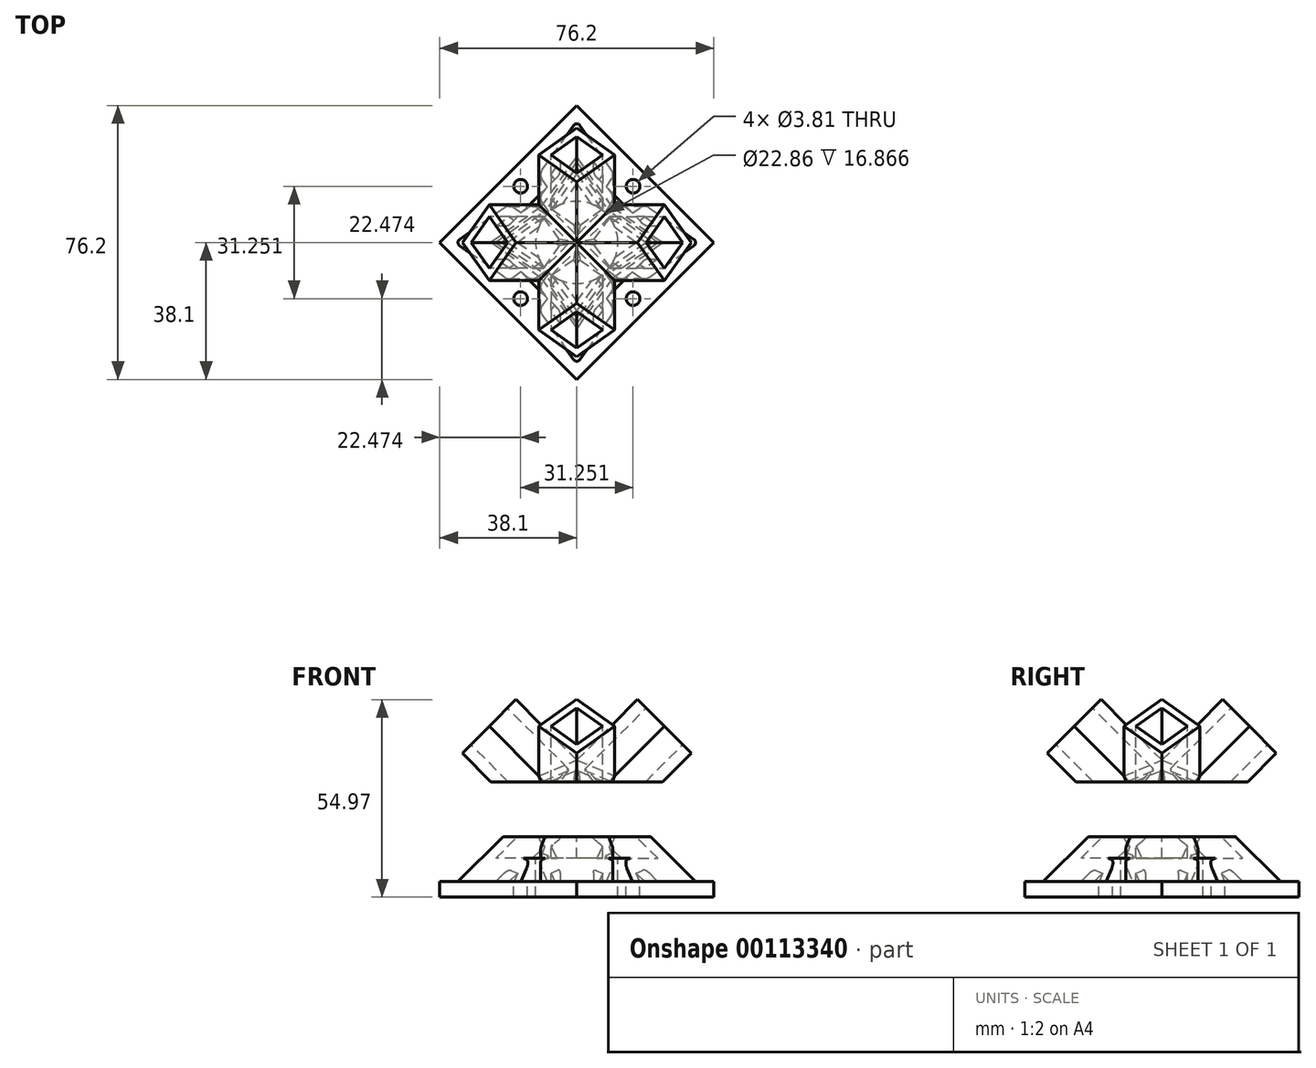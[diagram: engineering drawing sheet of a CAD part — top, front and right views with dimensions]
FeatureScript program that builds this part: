
annotation { "Feature Type Name" : "Feature", "Feature Type Description" : "" }
export const myFeature = defineFeature(function(context is Context, id is Id, definition is map)
    precondition{}
    {
        {
            var Q0;
            Q0=qCreatedBy(makeId("Top.planeOp"),FACE);
            var sketch = newSketch(context, id + "F0", { "sketchPlane" : qUnion([Q0])});
            skLineSegment(sketch, "E0", {"start": v(0, 0) * mm, "end": v(0, 35.93) * mm, "construction": true});
            skLineSegment(sketch, "E1", {"start": v(0, 0) * mm, "end": v(30.29, 0) * mm, "construction": true});
            skLineSegment(sketch, "E2", {"start": v(0, 0) * mm, "end": v(34.43, 34.43) * mm, "construction": true});
            skLineSegment(sketch, "E3", {"start": v(0, 38.1) * mm, "end": v(38.1, 0) * mm});
            skLineSegment(sketch, "E4", {"start": v(38.1, 0) * mm, "end": v(0, -38.1) * mm});
            skLineSegment(sketch, "E5", {"start": v(0, -38.1) * mm, "end": v(-38.1, 0) * mm});
            skLineSegment(sketch, "E6", {"start": v(-38.1, 0) * mm, "end": v(0, 38.1) * mm});
            skSolve(sketch);
        }
        {
            var Q0;
            Q0 = qSketchRegion(id + "F0", true);
            extrude(context, id + "F1", {"entities" : qUnion([Q0]), "depth" : 4.32 * mm});
        }
        {
            var Q0;
            Q0=sQuery(id+"F0.wireOp",EDGE,"E1");
            var Q1;
            Q1=qCreatedBy(makeId("Top.planeOp"),FACE);
            cPlane(context, id + "F2", {"entities" : qUnion([Q0, Q1]), "cplaneType" : CPlaneType.LINE_ANGLE, "offset" : 25.4 * mm, "angle" : 45 * degree, "width" : 152.4 * mm, "height" : 152.4 * mm});
        }
        {
            var Q0;
            Q0=qCreatedBy(id+"F2.planeOp",FACE);
            cPlane(context, id + "F3", {"entities" : qUnion([Q0]), "cplaneType" : CPlaneType.OFFSET, "offset" : 50.8 * mm, "oppositeDirection" : true, "width" : 152.4 * mm, "height" : 152.4 * mm});
        }
        {
            var Q0;
            Q0=qCreatedBy(makeId("Right.planeOp"),FACE);
            var sketch = newSketch(context, id + "F4", { "sketchPlane" : qUnion([Q0])});
            skLineSegment(sketch, "E7", {"start": v(0, 0) * mm, "end": v(0, 27.83) * mm, "construction": true});
            skLineSegment(sketch, "E8", {"start": v(-38.1, 0) * mm, "end": v(-56.06, 17.96) * mm, "construction": true});
            skSolve(sketch);
        }
        {
            var Q0;
            Q0=qCreatedBy(id+"F3.planeOp",FACE);
            var sketch = newSketch(context, id + "F5", { "sketchPlane" : qUnion([Q0])});
            skLineSegment(sketch, "E9", {"start": v(0, 26.94) * mm, "end": v(-10.56, 16.38) * mm});
            skLineSegment(sketch, "E10", {"start": v(0, 26.94) * mm, "end": v(0, 0) * mm, "construction": true});
            skLineSegment(sketch, "E11", {"start": v(-10.56, 16.38) * mm, "end": v(0, 5.82) * mm});
            skLineSegment(sketch, "E12", {"start": v(0, 26.94) * mm, "end": v(10.56, 16.38) * mm});
            skLineSegment(sketch, "E13", {"start": v(10.56, 16.38) * mm, "end": v(0, 5.82) * mm});
            skLineSegment(sketch, "E14", {"start": v(0, 23.56) * mm, "end": v(7.18, 16.38) * mm});
            skLineSegment(sketch, "E15", {"start": v(7.18, 16.38) * mm, "end": v(0, 9.2) * mm});
            skLineSegment(sketch, "E16", {"start": v(0, 9.2) * mm, "end": v(-7.18, 16.38) * mm});
            skLineSegment(sketch, "E17", {"start": v(-7.18, 16.38) * mm, "end": v(0, 23.56) * mm});
            skSolve(sketch);
        }
        {
            var Q0;
            Q0=makeQuery(id+"F5.imprint","IMPRINT",FACE,{"disambiguationData":[TD([[makeQuery(id+"F5.imprint","IMPRINT",EDGE,{"derivedFrom":sQuery(id+"F5.wireOp",EDGE,"E9")}),1.0]])]});
            extrude(context, id + "F6", {"entities" : qUnion([Q0]), "operationType" : NewBodyOperationType.ADD, "endBound" : BoundingType.UP_TO_NEXT, "depth" : 25.4 * mm});
        }
        {
            var Q0;
            Q0=makeQuery(id+"F6.opExtrude","SWEPT_FACE",FACE,{"disambiguationData":[OSD([sQuery(id+"F5.wireOp",EDGE,"E11")])]});
            cPlane(context, id + "F7", {"entities" : qUnion([Q0]), "cplaneType" : CPlaneType.OFFSET, "offset" : 0 * mm, "width" : 152.4 * mm, "height" : 152.4 * mm});
        }
        {
            var Q0;
            Q0=qCreatedBy(id+"F7.planeOp",FACE);
            var sketch = newSketch(context, id + "F8", { "sketchPlane" : qUnion([Q0])});
            skLineSegment(sketch, "E18", {"start": v(30.54, 7.4) * mm, "end": v(48.17, 19.87) * mm, "construction": true});
            skCircle(sketch, "E19.cCircle", {"center": v(30.54, 7.4) * mm, "radius": 1.65 * mm, "construction": true});
            skLineSegment(sketch, "E19.0", {"start": v(32.27, 6.6) * mm, "end": v(30.71, 5.5) * mm});
            skLineSegment(sketch, "E19.1", {"start": v(30.71, 5.5) * mm, "end": v(28.98, 6.3) * mm});
            skLineSegment(sketch, "E19.2", {"start": v(28.98, 6.3) * mm, "end": v(28.8, 8.2) * mm});
            skLineSegment(sketch, "E19.3", {"start": v(28.8, 8.2) * mm, "end": v(30.36, 9.3) * mm});
            skLineSegment(sketch, "E19.4", {"start": v(30.36, 9.3) * mm, "end": v(32.1, 8.5) * mm});
            skLineSegment(sketch, "E19.5", {"start": v(32.1, 8.5) * mm, "end": v(32.27, 6.6) * mm});
            skPoint(sketch, "E19.0.midPoint", {"position": v(31.5, 6.06) * mm});
            skSolve(sketch);
        }
        {
            var Q0;
            Q0 = qSketchRegion(id + "F8", true);
            extrude(context, id + "F9", {"entities" : qUnion([Q0]), "operationType" : NewBodyOperationType.REMOVE, "oppositeDirection" : true, "depth" : 2.54 * mm});
        }
        {
            var Q0;
            Q0=makeQuery(id+"F1.opExtrude","SWEPT_BODY",BODY,{"disambiguationData":[OSD([sQuery(id+"F0.wireOp",EDGE,"E3"),sQuery(id+"F0.wireOp",EDGE,"E4"),sQuery(id+"F0.wireOp",EDGE,"E5"),sQuery(id+"F0.wireOp",EDGE,"E6")])]});
            var Q1;
            Q1=sQuery(id+"F4.wireOp",EDGE,"E7");
            circularPattern(context, id + "F10", {"entities" : qUnion([Q0]), "axis" : qUnion([Q1]), "angle" : 90 * degree, "instanceCount" : 4});
        }
        {
            var Q0;
            Q0=qCreatedBy(makeId("Top.planeOp"),FACE);
            cPlane(context, id + "F11", {"entities" : qUnion([Q0]), "cplaneType" : CPlaneType.OFFSET, "offset" : 25.4 * mm, "width" : 152.4 * mm, "height" : 152.4 * mm});
        }
        {
            var Q0;
            Q0=qCreatedBy(id+"F11.planeOp",FACE);
            var sketch = newSketch(context, id + "F12", { "sketchPlane" : qUnion([Q0])});
            skCircle(sketch, "E20", {"center": v(0, 0) * mm, "radius": 11.43 * mm});
            skSolve(sketch);
        }
        {
            var Q0;
            Q0=qCreatedBy(makeId("Top.planeOp"),FACE);
            var sketch = newSketch(context, id + "F13", { "sketchPlane" : qUnion([Q0])});
            skLineSegment(sketch, "E21.bottom", {"start": v(19.05, 19.05) * mm, "end": v(-19.05, 19.05) * mm});
            skLineSegment(sketch, "E21.top", {"start": v(19.05, -19.05) * mm, "end": v(-19.05, -19.05) * mm});
            skLineSegment(sketch, "E21.left", {"start": v(19.05, 19.05) * mm, "end": v(19.05, -19.05) * mm});
            skLineSegment(sketch, "E21.right", {"start": v(-19.05, 19.05) * mm, "end": v(-19.05, -19.05) * mm});
            skPoint(sketch, "E21.middle", {"position": v(0, 0) * mm});
            skLineSegment(sketch, "E22", {"start": v(-19.05, 4.6) * mm, "end": v(-4.6, 19.05) * mm});
            skLineSegment(sketch, "E23", {"start": v(-19.05, -4.6) * mm, "end": v(-4.6, -19.05) * mm});
            skLineSegment(sketch, "E24", {"start": v(4.6, 19.05) * mm, "end": v(19.05, 4.6) * mm});
            skLineSegment(sketch, "E25", {"start": v(4.6, -19.05) * mm, "end": v(19.05, -4.6) * mm});
            skSolve(sketch);
        }
        {
            var Q0;
            {var subQ3=sQuery(id+"F13.wireOp",EDGE,"E22");Q0=makeQuery(id+"F13.imprint","IMPRINT",FACE,{"disambiguationData":[TD([[makeQuery(id+"F13.imprint","IMPRINT",EDGE,{"derivedFrom":subQ3}),-1.0]])]});}
            extrude(context, id + "F14", {"entities" : qUnion([Q0]), "depth" : 10.8 * mm});
        }
        {
            var Q0;
            Q0 = qSketchRegion(id + "F12", true);
            extrude(context, id + "F15", {"entities" : qUnion([Q0]), "operationType" : NewBodyOperationType.REMOVE, "oppositeDirection" : true, "depth" : 25.4 * mm});
        }
        {
            var Q0;
            Q0=qCreatedBy(id+"F11.planeOp",FACE);
            var sketch = newSketch(context, id + "F16", { "sketchPlane" : qUnion([Q0])});
            skCircle(sketch, "E26", {"center": v(0, 0) * mm, "radius": 22.1 * mm, "construction": true});
            skLineSegment(sketch, "E27", {"start": v(0, 0) * mm, "end": v(0, 32.05) * mm, "construction": true});
            skLineSegment(sketch, "E28", {"start": v(0, 0) * mm, "end": v(26.77, 26.77) * mm, "construction": true});
            skCircle(sketch, "E29", {"center": v(15.63, 15.63) * mm, "radius": 1.9 * mm});
            skCircle(sketch, "E30.1.0", {"center": v(-15.63, 15.63) * mm, "radius": 1.9 * mm});
            skCircle(sketch, "E30.2.0", {"center": v(-15.63, -15.63) * mm, "radius": 1.9 * mm});
            skCircle(sketch, "E30.3.0", {"center": v(15.63, -15.63) * mm, "radius": 1.9 * mm});
            skLineSegment(sketch, "E31", {"start": v(0, 0) * mm, "end": v(-26.06, 26.06) * mm, "construction": true});
            skSolve(sketch);
        }
        {
            var Q0;
            Q0=makeQuery(id+"F16.imprint","IMPRINT",FACE,{"disambiguationData":[TD([[makeQuery(id+"F16.imprint","IMPRINT",EDGE,{"derivedFrom":sQuery(id+"F16.wireOp",EDGE,"E30.1.0")}),1.0]])]});
            var Q1;
            Q1=makeQuery(id+"F16.imprint","IMPRINT",FACE,{"disambiguationData":[TD([[makeQuery(id+"F16.imprint","IMPRINT",EDGE,{"derivedFrom":sQuery(id+"F16.wireOp",EDGE,"E29")}),1.0]])]});
            var Q2;
            Q2=makeQuery(id+"F16.imprint","IMPRINT",FACE,{"disambiguationData":[TD([[makeQuery(id+"F16.imprint","IMPRINT",EDGE,{"derivedFrom":sQuery(id+"F16.wireOp",EDGE,"E30.3.0")}),1.0]])]});
            var Q3;
            Q3=makeQuery(id+"F16.imprint","IMPRINT",FACE,{"disambiguationData":[TD([[makeQuery(id+"F16.imprint","IMPRINT",EDGE,{"derivedFrom":sQuery(id+"F16.wireOp",EDGE,"E30.2.0")}),1.0]])]});
            extrude(context, id + "F17", {"entities" : qUnion([Q0, Q1, Q2, Q3]), "operationType" : NewBodyOperationType.REMOVE, "oppositeDirection" : true, "depth" : 25.4 * mm});
        }
        {
            var Q0;
            Q0=makeQuery(id+"F10.opPattern","COPY",BODY,{"derivedFrom":makeQuery(id+"F1.opExtrude","SWEPT_BODY",BODY,{"disambiguationData":[OSD([sQuery(id+"F0.wireOp",EDGE,"E3"),sQuery(id+"F0.wireOp",EDGE,"E4"),sQuery(id+"F0.wireOp",EDGE,"E5"),sQuery(id+"F0.wireOp",EDGE,"E6")])]}),"instanceName":"2"});
            var Q1;
            Q1=makeQuery(id+"F14.opExtrude","SWEPT_BODY",BODY,{"disambiguationData":[OSD([sQuery(id+"F13.wireOp",EDGE,"E21.bottom"),sQuery(id+"F13.wireOp",EDGE,"E21.top"),sQuery(id+"F13.wireOp",EDGE,"E21.left"),sQuery(id+"F13.wireOp",EDGE,"E21.right"),sQuery(id+"F13.wireOp",EDGE,"E22"),sQuery(id+"F13.wireOp",EDGE,"E23"),sQuery(id+"F13.wireOp",EDGE,"E24"),sQuery(id+"F13.wireOp",EDGE,"E25")])]});
            booleanBodies(context, id + "F18", {"operationType" : BooleanOperationType.UNION, "tools" : qUnion([Q0, Q1])});
        }
        {
            var Q0;
            Q0=makeQuery(id+"F10.opPattern","COPY",BODY,{"derivedFrom":makeQuery(id+"F1.opExtrude","SWEPT_BODY",BODY,{"disambiguationData":[OSD([sQuery(id+"F0.wireOp",EDGE,"E3"),sQuery(id+"F0.wireOp",EDGE,"E4"),sQuery(id+"F0.wireOp",EDGE,"E5"),sQuery(id+"F0.wireOp",EDGE,"E6")])]}),"instanceName":"2"});
            var Q1;
            Q1=makeQuery(id+"F10.opPattern","COPY",BODY,{"derivedFrom":makeQuery(id+"F1.opExtrude","SWEPT_BODY",BODY,{"disambiguationData":[OSD([sQuery(id+"F0.wireOp",EDGE,"E3"),sQuery(id+"F0.wireOp",EDGE,"E4"),sQuery(id+"F0.wireOp",EDGE,"E5"),sQuery(id+"F0.wireOp",EDGE,"E6")])]}),"instanceName":"3"});
            var Q2;
            Q2=makeQuery(id+"F1.opExtrude","SWEPT_BODY",BODY,{"disambiguationData":[OSD([sQuery(id+"F0.wireOp",EDGE,"E3"),sQuery(id+"F0.wireOp",EDGE,"E4"),sQuery(id+"F0.wireOp",EDGE,"E5"),sQuery(id+"F0.wireOp",EDGE,"E6")])]});
            var Q3;
            Q3=makeQuery(id+"F10.opPattern","COPY",BODY,{"derivedFrom":makeQuery(id+"F1.opExtrude","SWEPT_BODY",BODY,{"disambiguationData":[OSD([sQuery(id+"F0.wireOp",EDGE,"E3"),sQuery(id+"F0.wireOp",EDGE,"E4"),sQuery(id+"F0.wireOp",EDGE,"E5"),sQuery(id+"F0.wireOp",EDGE,"E6")])]}),"instanceName":"1"});
            booleanBodies(context, id + "F19", {"operationType" : BooleanOperationType.UNION, "tools" : qUnion([Q0, Q1, Q2, Q3])});
        }
        {
            var Q0;
            {var subQ4=makeQuery(id+"F6.opExtrude","SWEPT_FACE",FACE,{"disambiguationData":[OSD([sQuery(id+"F5.wireOp",EDGE,"E11")])]});var subQ6=sQuery(id+"F13.wireOp",EDGE,"E21.right");Q0=makeQuery(id+"F19.opBoolean","SPLIT",FACE,{"disambiguationData":[TD([makeQuery(id+"F10.opPattern","COPY",FACE,{"derivedFrom":subQ4,"instanceName":"3"})])],"derivedFrom":makeQuery(id+"F14.opExtrude","SWEPT_FACE",FACE,{"disambiguationData":[OSD([subQ6])]})});}
            var Q1;
            {var subQ4=makeQuery(id+"F6.opExtrude","SWEPT_FACE",FACE,{"disambiguationData":[OSD([sQuery(id+"F5.wireOp",EDGE,"E13")])]});var subQ6=sQuery(id+"F13.wireOp",EDGE,"E21.right");Q1=makeQuery(id+"F19.opBoolean","SPLIT",FACE,{"disambiguationData":[TD([makeQuery(id+"F10.opPattern","COPY",FACE,{"derivedFrom":subQ4,"instanceName":"3"})])],"derivedFrom":makeQuery(id+"F14.opExtrude","SWEPT_FACE",FACE,{"disambiguationData":[OSD([subQ6])]})});}
            extrude(context, id + "F20", {"entities" : qUnion([Q0, Q1]), "operationType" : NewBodyOperationType.ADD, "endBound" : BoundingType.UP_TO_NEXT, "depth" : 25.4 * mm});
        }
        {
            var Q0;
            {var subQ0=makeQuery(id+"F6.opExtrude","SWEPT_FACE",FACE,{"disambiguationData":[OSD([sQuery(id+"F5.wireOp",EDGE,"E13")])]});var subQ6=sQuery(id+"F13.wireOp",EDGE,"E21.bottom");Q0=makeQuery(id+"F18.opBoolean","SPLIT",FACE,{"disambiguationData":[TD([makeQuery(id+"F10.opPattern","COPY",FACE,{"derivedFrom":subQ0,"instanceName":"2"})])],"derivedFrom":makeQuery(id+"F14.opExtrude","SWEPT_FACE",FACE,{"disambiguationData":[OSD([subQ6])]})});}
            var Q1;
            {var subQ4=makeQuery(id+"F6.opExtrude","SWEPT_FACE",FACE,{"disambiguationData":[OSD([sQuery(id+"F5.wireOp",EDGE,"E11")])]});var subQ6=sQuery(id+"F13.wireOp",EDGE,"E21.bottom");Q1=makeQuery(id+"F18.opBoolean","SPLIT",FACE,{"disambiguationData":[TD([makeQuery(id+"F10.opPattern","COPY",FACE,{"derivedFrom":subQ4,"instanceName":"2"})])],"derivedFrom":makeQuery(id+"F14.opExtrude","SWEPT_FACE",FACE,{"disambiguationData":[OSD([subQ6])]})});}
            extrude(context, id + "F21", {"entities" : qUnion([Q0, Q1]), "operationType" : NewBodyOperationType.ADD, "endBound" : BoundingType.UP_TO_NEXT, "depth" : 25.4 * mm});
        }
        {
            var Q0;
            {var subQ0=makeQuery(id+"F6.opExtrude","SWEPT_FACE",FACE,{"disambiguationData":[OSD([sQuery(id+"F5.wireOp",EDGE,"E11")])]});var subQ6=sQuery(id+"F13.wireOp",EDGE,"E21.left");Q0=makeQuery(id+"F19.opBoolean","SPLIT",FACE,{"disambiguationData":[TD([makeQuery(id+"F10.opPattern","COPY",FACE,{"derivedFrom":subQ0,"instanceName":"1"})])],"derivedFrom":makeQuery(id+"F14.opExtrude","SWEPT_FACE",FACE,{"disambiguationData":[OSD([subQ6])]})});}
            var Q1;
            {var subQ0=makeQuery(id+"F6.opExtrude","SWEPT_FACE",FACE,{"disambiguationData":[OSD([sQuery(id+"F5.wireOp",EDGE,"E13")])]});var subQ6=sQuery(id+"F13.wireOp",EDGE,"E21.left");Q1=makeQuery(id+"F19.opBoolean","SPLIT",FACE,{"disambiguationData":[TD([makeQuery(id+"F10.opPattern","COPY",FACE,{"derivedFrom":subQ0,"instanceName":"1"})])],"derivedFrom":makeQuery(id+"F14.opExtrude","SWEPT_FACE",FACE,{"disambiguationData":[OSD([subQ6])]})});}
            extrude(context, id + "F22", {"entities" : qUnion([Q0, Q1]), "operationType" : NewBodyOperationType.ADD, "endBound" : BoundingType.UP_TO_NEXT, "depth" : 25.4 * mm});
        }
        {
            var Q0;
            {var subQ0=makeQuery(id+"F6.opExtrude","SWEPT_FACE",FACE,{"disambiguationData":[OSD([sQuery(id+"F5.wireOp",EDGE,"E13")])]});var subQ2=sQuery(id+"F13.wireOp",EDGE,"E21.top");Q0=makeQuery(id+"F19.opBoolean","SPLIT",FACE,{"disambiguationData":[TD([subQ0])],"derivedFrom":makeQuery(id+"F14.opExtrude","SWEPT_FACE",FACE,{"disambiguationData":[OSD([subQ2])]})});}
            var Q1;
            {var subQ0=makeQuery(id+"F6.opExtrude","SWEPT_FACE",FACE,{"disambiguationData":[OSD([sQuery(id+"F5.wireOp",EDGE,"E11")])]});var subQ6=sQuery(id+"F13.wireOp",EDGE,"E21.top");Q1=makeQuery(id+"F19.opBoolean","SPLIT",FACE,{"disambiguationData":[TD([subQ0])],"derivedFrom":makeQuery(id+"F14.opExtrude","SWEPT_FACE",FACE,{"disambiguationData":[OSD([subQ6])]})});}
            extrude(context, id + "F23", {"entities" : qUnion([Q0, Q1]), "operationType" : NewBodyOperationType.ADD, "endBound" : BoundingType.UP_TO_NEXT, "depth" : 25.4 * mm});
        }
        {
            var Q0;
            Q0=qCreatedBy(makeId("Right.planeOp"),FACE);
            cPlane(context, id + "F24", {"entities" : qUnion([Q0]), "cplaneType" : CPlaneType.OFFSET, "offset" : 63.5 * mm, "width" : 152.4 * mm, "height" : 152.4 * mm});
        }
        {
            var Q0;
            Q0=qCreatedBy(id+"F24.planeOp",FACE);
            var sketch = newSketch(context, id + "F25", { "sketchPlane" : qUnion([Q0])});
            skLineSegment(sketch, "E32.bottom", {"start": v(-55.88, 16.87) * mm, "end": v(55.88, 16.87) * mm});
            skLineSegment(sketch, "E32.top", {"start": v(-55.88, 32.1) * mm, "end": v(55.88, 32.1) * mm});
            skLineSegment(sketch, "E32.left", {"start": v(-55.88, 16.87) * mm, "end": v(-55.88, 32.1) * mm});
            skLineSegment(sketch, "E32.right", {"start": v(55.88, 16.87) * mm, "end": v(55.88, 32.1) * mm});
            skSolve(sketch);
        }
        {
            var Q0;
            Q0 = qSketchRegion(id + "F25", true);
            extrude(context, id + "F26", {"entities" : qUnion([Q0]), "operationType" : NewBodyOperationType.REMOVE, "oppositeDirection" : true, "depth" : 152.4 * mm});
        }
        {
            var Q0;
            Q0=makeQuery(id+"F10.opPattern","COPY",EDGE,{"derivedFrom":makeQuery(id+"F6.opExtrude","SWEPT_EDGE",EDGE,{"disambiguationData":[OSD([sQuery(id+"F5.wireOp",EDGE,"E11"),sQuery(id+"F5.wireOp",EDGE,"E13")])]}),"instanceName":"2"});
            var Q1;
            Q1=makeQuery(id+"F10.opPattern","COPY",EDGE,{"derivedFrom":makeQuery(id+"F6.opExtrude","SWEPT_EDGE",EDGE,{"disambiguationData":[OSD([sQuery(id+"F5.wireOp",EDGE,"E9"),sQuery(id+"F5.wireOp",EDGE,"E11")])]}),"instanceName":"2"});
            var Q2;
            Q2=makeQuery(id+"F10.opPattern","COPY",EDGE,{"derivedFrom":makeQuery(id+"F6.opExtrude","SWEPT_EDGE",EDGE,{"disambiguationData":[OSD([sQuery(id+"F5.wireOp",EDGE,"E9"),sQuery(id+"F5.wireOp",EDGE,"E12")])]}),"instanceName":"2"});
            var Q3;
            Q3=makeQuery(id+"F10.opPattern","COPY",EDGE,{"derivedFrom":makeQuery(id+"F6.opExtrude","SWEPT_EDGE",EDGE,{"disambiguationData":[OSD([sQuery(id+"F5.wireOp",EDGE,"E12"),sQuery(id+"F5.wireOp",EDGE,"E13")])]}),"instanceName":"2"});
            var Q4;
            Q4=makeQuery(id+"F10.opPattern","COPY",EDGE,{"derivedFrom":makeQuery(id+"F6.opExtrude","SWEPT_EDGE",EDGE,{"disambiguationData":[OSD([sQuery(id+"F5.wireOp",EDGE,"E12"),sQuery(id+"F5.wireOp",EDGE,"E13")])]}),"instanceName":"1"});
            var Q5;
            Q5=makeQuery(id+"F10.opPattern","COPY",EDGE,{"derivedFrom":makeQuery(id+"F6.opExtrude","SWEPT_EDGE",EDGE,{"disambiguationData":[OSD([sQuery(id+"F5.wireOp",EDGE,"E9"),sQuery(id+"F5.wireOp",EDGE,"E12")])]}),"instanceName":"1"});
            var Q6;
            Q6=makeQuery(id+"F10.opPattern","COPY",EDGE,{"derivedFrom":makeQuery(id+"F6.opExtrude","SWEPT_EDGE",EDGE,{"disambiguationData":[OSD([sQuery(id+"F5.wireOp",EDGE,"E9"),sQuery(id+"F5.wireOp",EDGE,"E11")])]}),"instanceName":"1"});
            var Q7;
            Q7=makeQuery(id+"F10.opPattern","COPY",EDGE,{"derivedFrom":makeQuery(id+"F6.opExtrude","SWEPT_EDGE",EDGE,{"disambiguationData":[OSD([sQuery(id+"F5.wireOp",EDGE,"E11"),sQuery(id+"F5.wireOp",EDGE,"E13")])]}),"instanceName":"1"});
            fillet(context, id + "F27", {"entities" : qUnion([Q0, Q1, Q2, Q3, Q4, Q5, Q6, Q7]), "radius" : 1.27 * mm, "tangentPropagation" : true, "allowEdgeOverflow" : false});
        }
        {
            var Q0;
            Q0=makeQuery(id+"F6.opExtrude","SWEPT_EDGE",EDGE,{"disambiguationData":[OSD([sQuery(id+"F5.wireOp",EDGE,"E9"),sQuery(id+"F5.wireOp",EDGE,"E11")])]});
            var Q1;
            Q1=makeQuery(id+"F6.opExtrude","SWEPT_EDGE",EDGE,{"disambiguationData":[OSD([sQuery(id+"F5.wireOp",EDGE,"E9"),sQuery(id+"F5.wireOp",EDGE,"E12")])]});
            var Q2;
            Q2=makeQuery(id+"F6.opExtrude","SWEPT_EDGE",EDGE,{"disambiguationData":[OSD([sQuery(id+"F5.wireOp",EDGE,"E12"),sQuery(id+"F5.wireOp",EDGE,"E13")])]});
            var Q3;
            Q3=makeQuery(id+"F6.opExtrude","SWEPT_EDGE",EDGE,{"disambiguationData":[OSD([sQuery(id+"F5.wireOp",EDGE,"E11"),sQuery(id+"F5.wireOp",EDGE,"E13")])]});
            var Q4;
            Q4=makeQuery(id+"F10.opPattern","COPY",EDGE,{"derivedFrom":makeQuery(id+"F6.opExtrude","SWEPT_EDGE",EDGE,{"disambiguationData":[OSD([sQuery(id+"F5.wireOp",EDGE,"E11"),sQuery(id+"F5.wireOp",EDGE,"E13")])]}),"instanceName":"3"});
            var Q5;
            Q5=makeQuery(id+"F10.opPattern","COPY",EDGE,{"derivedFrom":makeQuery(id+"F6.opExtrude","SWEPT_EDGE",EDGE,{"disambiguationData":[OSD([sQuery(id+"F5.wireOp",EDGE,"E12"),sQuery(id+"F5.wireOp",EDGE,"E13")])]}),"instanceName":"3"});
            var Q6;
            Q6=makeQuery(id+"F10.opPattern","COPY",EDGE,{"derivedFrom":makeQuery(id+"F6.opExtrude","SWEPT_EDGE",EDGE,{"disambiguationData":[OSD([sQuery(id+"F5.wireOp",EDGE,"E9"),sQuery(id+"F5.wireOp",EDGE,"E11")])]}),"instanceName":"3"});
            var Q7;
            Q7=makeQuery(id+"F10.opPattern","COPY",EDGE,{"derivedFrom":makeQuery(id+"F6.opExtrude","SWEPT_EDGE",EDGE,{"disambiguationData":[OSD([sQuery(id+"F5.wireOp",EDGE,"E9"),sQuery(id+"F5.wireOp",EDGE,"E12")])]}),"instanceName":"3"});
            fillet(context, id + "F28", {"entities" : qUnion([Q0, Q1, Q2, Q3, Q4, Q5, Q6, Q7]), "radius" : 1.27 * mm, "tangentPropagation" : true, "allowEdgeOverflow" : false});
        }
        {
            var Q0;
            Q0=makeQuery(id+"F22.opExtrude","TWEAK_EDGE",EDGE,{"derivedFrom":[makeQuery(id+"F14.opExtrude","SWEPT_EDGE",EDGE,{"disambiguationData":[OSD([sQuery(id+"F13.wireOp",EDGE,"E21.left"),sQuery(id+"F13.wireOp",EDGE,"E24")])]}),makeQuery(id+"F10.opPattern","COPY",FACE,{"derivedFrom":makeQuery(id+"F6.opExtrude","SWEPT_FACE",FACE,{"disambiguationData":[OSD([sQuery(id+"F5.wireOp",EDGE,"E13")])]}),"instanceName":"1"})]});
            var Q1;
            {var subQ0=sQuery(id+"F13.wireOp",EDGE,"E24");var subQ1=sQuery(id+"F13.wireOp",EDGE,"E21.left");Q1=makeQuery(id+"F22.boolean.opBoolean","MERGE",EDGE,{"derivedFrom":[makeQuery(id+"F14.opExtrude","SWEPT_EDGE",EDGE,{"disambiguationData":[OSD([subQ1,subQ0])]}),makeQuery(id+"F22.opExtrude","CAP_EDGE",EDGE,{"disambiguationData":[OSD([subQ1,subQ0])],"isStart":true})]});}
            var Q2;
            {var subQ0=sQuery(id+"F13.wireOp",EDGE,"E24");var subQ1=sQuery(id+"F13.wireOp",EDGE,"E21.bottom");Q2=makeQuery(id+"F21.boolean.opBoolean","MERGE",EDGE,{"derivedFrom":[makeQuery(id+"F14.opExtrude","SWEPT_EDGE",EDGE,{"disambiguationData":[OSD([subQ1,subQ0])]}),makeQuery(id+"F21.opExtrude","CAP_EDGE",EDGE,{"disambiguationData":[OSD([subQ1,subQ0])],"isStart":true})]});}
            var Q3;
            Q3=makeQuery(id+"F21.opExtrude","TWEAK_EDGE",EDGE,{"derivedFrom":[makeQuery(id+"F14.opExtrude","SWEPT_EDGE",EDGE,{"disambiguationData":[OSD([sQuery(id+"F13.wireOp",EDGE,"E21.bottom"),sQuery(id+"F13.wireOp",EDGE,"E24")])]}),makeQuery(id+"F10.opPattern","COPY",FACE,{"derivedFrom":makeQuery(id+"F6.opExtrude","SWEPT_FACE",FACE,{"disambiguationData":[OSD([sQuery(id+"F5.wireOp",EDGE,"E11")])]}),"instanceName":"2"})]});
            var Q4;
            Q4=makeQuery(id+"F21.opExtrude","TWEAK_EDGE",EDGE,{"derivedFrom":[makeQuery(id+"F14.opExtrude","SWEPT_EDGE",EDGE,{"disambiguationData":[OSD([sQuery(id+"F13.wireOp",EDGE,"E21.bottom"),sQuery(id+"F13.wireOp",EDGE,"E22")])]}),makeQuery(id+"F10.opPattern","COPY",FACE,{"derivedFrom":makeQuery(id+"F6.opExtrude","SWEPT_FACE",FACE,{"disambiguationData":[OSD([sQuery(id+"F5.wireOp",EDGE,"E13")])]}),"instanceName":"2"})]});
            var Q5;
            {var subQ0=sQuery(id+"F13.wireOp",EDGE,"E22");var subQ1=sQuery(id+"F13.wireOp",EDGE,"E21.bottom");Q5=makeQuery(id+"F21.boolean.opBoolean","MERGE",EDGE,{"derivedFrom":[makeQuery(id+"F14.opExtrude","SWEPT_EDGE",EDGE,{"disambiguationData":[OSD([subQ1,subQ0])]}),makeQuery(id+"F21.opExtrude","CAP_EDGE",EDGE,{"disambiguationData":[OSD([subQ1,subQ0])],"isStart":true})]});}
            var Q6;
            {var subQ0=sQuery(id+"F13.wireOp",EDGE,"E22");var subQ1=sQuery(id+"F13.wireOp",EDGE,"E21.right");Q6=makeQuery(id+"F20.boolean.opBoolean","MERGE",EDGE,{"derivedFrom":[makeQuery(id+"F14.opExtrude","SWEPT_EDGE",EDGE,{"disambiguationData":[OSD([subQ1,subQ0])]}),makeQuery(id+"F20.opExtrude","CAP_EDGE",EDGE,{"disambiguationData":[OSD([subQ1,subQ0])],"isStart":true})]});}
            var Q7;
            Q7=makeQuery(id+"F20.opExtrude","TWEAK_EDGE",EDGE,{"derivedFrom":[makeQuery(id+"F14.opExtrude","SWEPT_EDGE",EDGE,{"disambiguationData":[OSD([sQuery(id+"F13.wireOp",EDGE,"E21.right"),sQuery(id+"F13.wireOp",EDGE,"E22")])]}),makeQuery(id+"F10.opPattern","COPY",FACE,{"derivedFrom":makeQuery(id+"F6.opExtrude","SWEPT_FACE",FACE,{"disambiguationData":[OSD([sQuery(id+"F5.wireOp",EDGE,"E11")])]}),"instanceName":"3"})]});
            var Q8;
            Q8=makeQuery(id+"F20.opExtrude","TWEAK_EDGE",EDGE,{"derivedFrom":[makeQuery(id+"F14.opExtrude","SWEPT_EDGE",EDGE,{"disambiguationData":[OSD([sQuery(id+"F13.wireOp",EDGE,"E21.right"),sQuery(id+"F13.wireOp",EDGE,"E23")])]}),makeQuery(id+"F10.opPattern","COPY",FACE,{"derivedFrom":makeQuery(id+"F6.opExtrude","SWEPT_FACE",FACE,{"disambiguationData":[OSD([sQuery(id+"F5.wireOp",EDGE,"E13")])]}),"instanceName":"3"})]});
            var Q9;
            {var subQ0=sQuery(id+"F13.wireOp",EDGE,"E23");var subQ1=sQuery(id+"F13.wireOp",EDGE,"E21.right");Q9=makeQuery(id+"F20.boolean.opBoolean","MERGE",EDGE,{"derivedFrom":[makeQuery(id+"F14.opExtrude","SWEPT_EDGE",EDGE,{"disambiguationData":[OSD([subQ1,subQ0])]}),makeQuery(id+"F20.opExtrude","CAP_EDGE",EDGE,{"disambiguationData":[OSD([subQ1,subQ0])],"isStart":true})]});}
            var Q10;
            {var subQ0=sQuery(id+"F13.wireOp",EDGE,"E23");var subQ1=sQuery(id+"F13.wireOp",EDGE,"E21.top");Q10=makeQuery(id+"F23.boolean.opBoolean","MERGE",EDGE,{"derivedFrom":[makeQuery(id+"F14.opExtrude","SWEPT_EDGE",EDGE,{"disambiguationData":[OSD([subQ1,subQ0])]}),makeQuery(id+"F23.opExtrude","CAP_EDGE",EDGE,{"disambiguationData":[OSD([subQ1,subQ0])],"isStart":true})]});}
            var Q11;
            Q11=makeQuery(id+"F23.opExtrude","TWEAK_EDGE",EDGE,{"derivedFrom":[makeQuery(id+"F14.opExtrude","SWEPT_EDGE",EDGE,{"disambiguationData":[OSD([sQuery(id+"F13.wireOp",EDGE,"E21.top"),sQuery(id+"F13.wireOp",EDGE,"E23")])]}),makeQuery(id+"F6.opExtrude","SWEPT_FACE",FACE,{"disambiguationData":[OSD([sQuery(id+"F5.wireOp",EDGE,"E11")])]})]});
            var Q12;
            Q12=makeQuery(id+"F23.opExtrude","TWEAK_EDGE",EDGE,{"derivedFrom":[makeQuery(id+"F14.opExtrude","SWEPT_EDGE",EDGE,{"disambiguationData":[OSD([sQuery(id+"F13.wireOp",EDGE,"E21.top"),sQuery(id+"F13.wireOp",EDGE,"E25")])]}),makeQuery(id+"F6.opExtrude","SWEPT_FACE",FACE,{"disambiguationData":[OSD([sQuery(id+"F5.wireOp",EDGE,"E13")])]})]});
            var Q13;
            {var subQ0=sQuery(id+"F13.wireOp",EDGE,"E25");var subQ1=sQuery(id+"F13.wireOp",EDGE,"E21.top");Q13=makeQuery(id+"F23.boolean.opBoolean","MERGE",EDGE,{"derivedFrom":[makeQuery(id+"F14.opExtrude","SWEPT_EDGE",EDGE,{"disambiguationData":[OSD([subQ1,subQ0])]}),makeQuery(id+"F23.opExtrude","CAP_EDGE",EDGE,{"disambiguationData":[OSD([subQ1,subQ0])],"isStart":true})]});}
            var Q14;
            {var subQ0=sQuery(id+"F13.wireOp",EDGE,"E25");var subQ1=sQuery(id+"F13.wireOp",EDGE,"E21.left");Q14=makeQuery(id+"F22.boolean.opBoolean","MERGE",EDGE,{"derivedFrom":[makeQuery(id+"F14.opExtrude","SWEPT_EDGE",EDGE,{"disambiguationData":[OSD([subQ1,subQ0])]}),makeQuery(id+"F22.opExtrude","CAP_EDGE",EDGE,{"disambiguationData":[OSD([subQ1,subQ0])],"isStart":true})]});}
            var Q15;
            Q15=makeQuery(id+"F22.opExtrude","TWEAK_EDGE",EDGE,{"derivedFrom":[makeQuery(id+"F14.opExtrude","SWEPT_EDGE",EDGE,{"disambiguationData":[OSD([sQuery(id+"F13.wireOp",EDGE,"E21.left"),sQuery(id+"F13.wireOp",EDGE,"E25")])]}),makeQuery(id+"F10.opPattern","COPY",FACE,{"derivedFrom":makeQuery(id+"F6.opExtrude","SWEPT_FACE",FACE,{"disambiguationData":[OSD([sQuery(id+"F5.wireOp",EDGE,"E11")])]}),"instanceName":"1"})]});
            fillet(context, id + "F29", {"entities" : qUnion([Q0, Q1, Q2, Q3, Q4, Q5, Q6, Q7, Q8, Q9, Q10, Q11, Q12, Q13, Q14, Q15]), "radius" : 2.54 * mm, "tangentPropagation" : true, "allowEdgeOverflow" : false});
        }
    });
